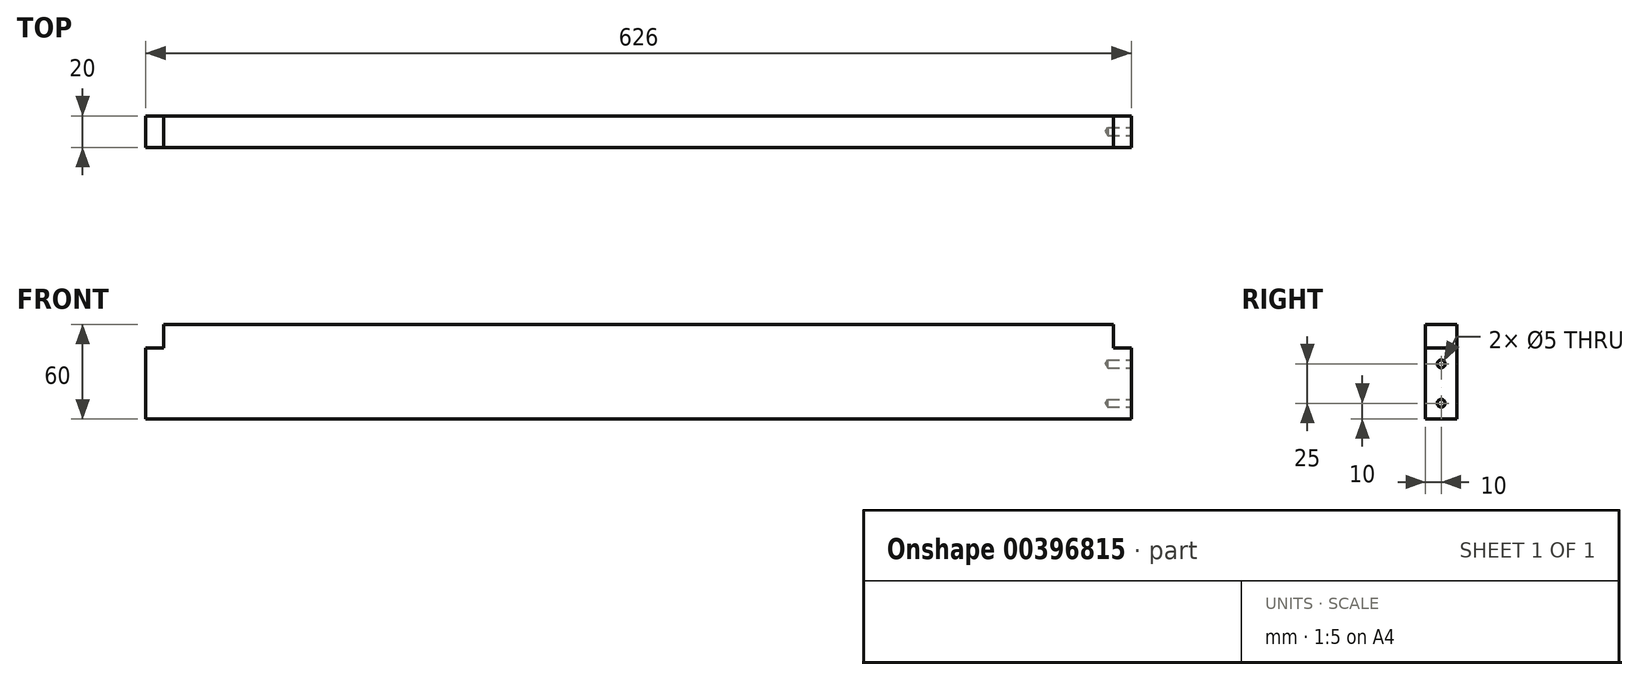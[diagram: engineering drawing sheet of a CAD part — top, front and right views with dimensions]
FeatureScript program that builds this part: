
annotation { "Feature Type Name" : "Feature", "Feature Type Description" : "" }
export const myFeature = defineFeature(function(context is Context, id is Id, definition is map)
    precondition{}
    {
        {
            var Q0;
            Q0=qCreatedBy(makeId("Front.planeOp"),FACE);
            var sketch = newSketch(context, id + "F0", { "sketchPlane" : qUnion([Q0])});
            skLineSegment(sketch, "E0", {"start": v(-313, 0) * mm, "end": v(313, 0) * mm});
            skLineSegment(sketch, "E1", {"start": v(313, 0) * mm, "end": v(313, 45) * mm});
            skLineSegment(sketch, "E2", {"start": v(313, 45) * mm, "end": v(301.5, 45) * mm});
            skLineSegment(sketch, "E3", {"start": v(301.5, 45) * mm, "end": v(301.5, 60) * mm});
            skLineSegment(sketch, "E4", {"start": v(301.5, 60) * mm, "end": v(-301.5, 60) * mm});
            skLineSegment(sketch, "E5", {"start": v(-301.5, 60) * mm, "end": v(-301.5, 45) * mm});
            skLineSegment(sketch, "E6", {"start": v(-301.5, 45) * mm, "end": v(-313, 45) * mm});
            skLineSegment(sketch, "E7", {"start": v(-313, 45) * mm, "end": v(-313, 0) * mm});
            skSolve(sketch);
        }
        {
            var Q0;
            Q0 = qSketchRegion(id + "F0", true);
            extrude(context, id + "F1", {"entities" : qUnion([Q0]), "endBound" : BoundingType.SYMMETRIC, "depth" : 20 * mm});
        }
        {
            var Q0;
            Q0=makeQuery(id+"F1.opExtrude","SWEPT_FACE",FACE,{"disambiguationData":[OSD([sQuery(id+"F0.wireOp",EDGE,"E1")])]});
            var sketch = newSketch(context, id + "F2", { "sketchPlane" : qUnion([Q0])});
            skPoint(sketch, "E8", {"position": v(0, 10) * mm});
            skPoint(sketch, "E9", {"position": v(0, 35) * mm});
            skSolve(sketch);
        }
        {
            var Q0;
            Q0=sQuery(id+"F2.wireOp",VERTEX,"E8");
            var Q1;
            Q1=sQuery(id+"F2.wireOp",VERTEX,"E9");
            var Q2;
            Q2=makeQuery(id+"F1.opExtrude","SWEPT_BODY",BODY,{"disambiguationData":[OSD([sQuery(id+"F0.wireOp",EDGE,"E0"),sQuery(id+"F0.wireOp",EDGE,"E1"),sQuery(id+"F0.wireOp",EDGE,"E2"),sQuery(id+"F0.wireOp",EDGE,"E3"),sQuery(id+"F0.wireOp",EDGE,"E4"),sQuery(id+"F0.wireOp",EDGE,"E5"),sQuery(id+"F0.wireOp",EDGE,"E6"),sQuery(id+"F0.wireOp",EDGE,"E7")])]});
            hole(context, id + "F3", {"style" : HoleStyle.SIMPLE, "endStyle" : HoleEndStyle.BLIND, "standardTappedOrClearance" : lookupTablePath({ "standard" : "ISO", "engagement" : "75%", "pitch" : "1 mm", "size" : "M6", "type" : "Tapped" }), "standardBlindInLast" : lookupTablePath({ "standard" : "ISO", "engagement" : "75%", "pitch" : "1 mm", "size" : "M6", "type" : "Tapped" }), "holeDiameter" : 5 * mm, "showTappedDepth" : true, "holeDepth" : 15 * mm, "isTappedThrough" : true, "tappedDepth" : 12 * mm, "tapClearance" : 3, "locations" : qUnion([Q0, Q1]), "scope" : qUnion([Q2]), "majorDiameter" : 6 * mm});
        }
    });
